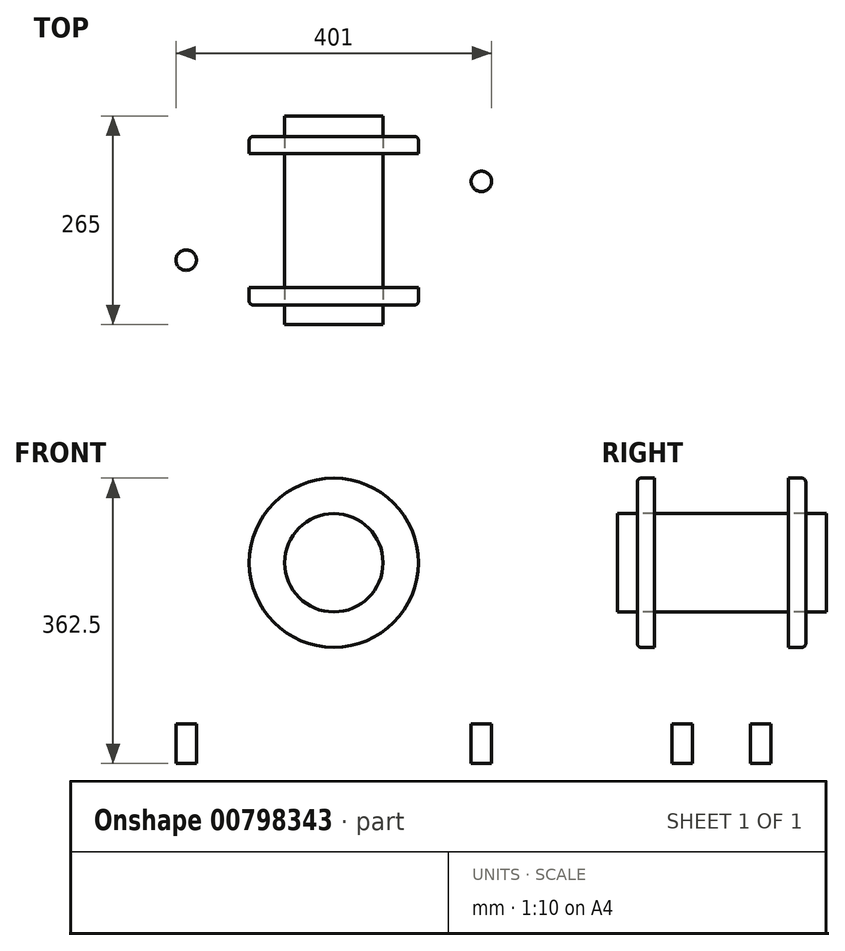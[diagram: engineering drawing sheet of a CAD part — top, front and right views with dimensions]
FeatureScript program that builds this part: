
annotation { "Feature Type Name" : "Feature", "Feature Type Description" : "" }
export const myFeature = defineFeature(function(context is Context, id is Id, definition is map)
    precondition{}
    {
        {
            var Q0;
            Q0=qCreatedBy(makeId("Front.planeOp"),FACE);
            var sketch = newSketch(context, id + "F0", { "sketchPlane" : qUnion([Q0])});
            skCircle(sketch, "E0", {"center": v(0, 0) * mm, "radius": 55 * mm});
            skLineSegment(sketch, "E1.bottom", {"start": v(0, 0) * mm, "end": v(-145, 0) * mm});
            skLineSegment(sketch, "E1.top", {"start": v(0, -255) * mm, "end": v(-225, -255) * mm});
            skLineSegment(sketch, "E1.left", {"start": v(0, 0) * mm, "end": v(0, -255) * mm});
            skLineSegment(sketch, "E1.right", {"start": v(-225, -205) * mm, "end": v(-225, -255) * mm});
            skLineSegment(sketch, "E2.bottom", {"start": v(0, 0) * mm, "end": v(145, 0) * mm});
            skLineSegment(sketch, "E2.top", {"start": v(0, -255) * mm, "end": v(225, -255) * mm});
            skLineSegment(sketch, "E2.right", {"start": v(225, -205) * mm, "end": v(225, -255) * mm});
            skCircle(sketch, "E3", {"center": v(0, 0) * mm, "radius": 90 * mm});
            skLineSegment(sketch, "E4", {"start": v(-145, 0) * mm, "end": v(-145, -205) * mm});
            skLineSegment(sketch, "E5", {"start": v(-145, -205) * mm, "end": v(-225, -205) * mm});
            skLineSegment(sketch, "E6", {"start": v(145, 0) * mm, "end": v(145, -205) * mm});
            skLineSegment(sketch, "E7", {"start": v(145, -205) * mm, "end": v(225, -205) * mm});
            skArc(sketch, "E8", {"start": v(145, 0) * mm, "mid": v(0, 125) * mm, "end": v(-145, 0) * mm});
            skSolve(sketch);
        }
        {
            var Q0;
            {var subQ1=sQuery(id+"F0.wireOp",EDGE,"E2.top");Q0=makeQuery(id+"F0.imprint","IMPRINT",FACE,{"disambiguationData":[TD([[makeQuery(id+"F0.imprint","IMPRINT",EDGE,{"derivedFrom":subQ1}),1.0]])]});}
            var Q1;
            {var subQ0=sQuery(id+"F0.wireOp",EDGE,"E8");Q1=makeQuery(id+"F0.imprint","IMPRINT",FACE,{"disambiguationData":[TD([[makeQuery(id+"F0.imprint","IMPRINT",EDGE,{"derivedFrom":subQ0}),1.0]])]});}
            var Q2;
            {var subQ0=sQuery(id+"F0.wireOp",EDGE,"E1.bottom");var subQ1=sQuery(id+"F0.wireOp",EDGE,"E0");var subQ2=makeQuery(id+"F0.imprint","INTERSECT",VERTEX,{"derivedFrom":[subQ1,subQ0]});Q2=makeQuery(id+"F0.imprint","IMPRINT",FACE,{"disambiguationData":[TD([[makeQuery(id+"F0.imprint","IMPRINT",EDGE,{"disambiguationData":[TD([[subQ2,1.0]])],"derivedFrom":subQ1}),-1.0]])]});}
            var Q3;
            {var subQ1=sQuery(id+"F0.wireOp",EDGE,"E1.top");Q3=makeQuery(id+"F0.imprint","IMPRINT",FACE,{"disambiguationData":[TD([[makeQuery(id+"F0.imprint","IMPRINT",EDGE,{"derivedFrom":subQ1}),-1.0]])]});}
            var Q4;
            {var subQ0=sQuery(id+"F0.wireOp",EDGE,"E1.bottom");var subQ1=sQuery(id+"F0.wireOp",EDGE,"E0");var subQ2=makeQuery(id+"F0.imprint","INTERSECT",VERTEX,{"derivedFrom":[subQ1,subQ0]});Q4=makeQuery(id+"F0.imprint","IMPRINT",FACE,{"disambiguationData":[TD([[makeQuery(id+"F0.imprint","IMPRINT",EDGE,{"disambiguationData":[TD([[subQ2,-1.0]])],"derivedFrom":subQ1}),-1.0]])]});}
            var Q5;
            {var subQ0=sQuery(id+"F0.wireOp",EDGE,"E2.bottom");var subQ1=sQuery(id+"F0.wireOp",EDGE,"E0");var subQ2=makeQuery(id+"F0.imprint","INTERSECT",VERTEX,{"derivedFrom":[subQ1,subQ0]});Q5=makeQuery(id+"F0.imprint","IMPRINT",FACE,{"disambiguationData":[TD([[makeQuery(id+"F0.imprint","IMPRINT",EDGE,{"disambiguationData":[TD([[subQ2,1.0]])],"derivedFrom":subQ1}),-1.0]])]});}
            var Q6;
            {var subQ0=sQuery(id+"F0.wireOp",EDGE,"E2.bottom");var subQ1=sQuery(id+"F0.wireOp",EDGE,"E0");var subQ2=makeQuery(id+"F0.imprint","INTERSECT",VERTEX,{"derivedFrom":[subQ1,subQ0]});Q6=makeQuery(id+"F0.imprint","IMPRINT",FACE,{"disambiguationData":[TD([[makeQuery(id+"F0.imprint","IMPRINT",EDGE,{"disambiguationData":[TD([[subQ2,1.0]])],"derivedFrom":subQ1}),1.0]])]});}
            var Q7;
            {var subQ0=sQuery(id+"F0.wireOp",EDGE,"E1.bottom");var subQ1=sQuery(id+"F0.wireOp",EDGE,"E0");var subQ2=makeQuery(id+"F0.imprint","INTERSECT",VERTEX,{"derivedFrom":[subQ1,subQ0]});Q7=makeQuery(id+"F0.imprint","IMPRINT",FACE,{"disambiguationData":[TD([[makeQuery(id+"F0.imprint","IMPRINT",EDGE,{"disambiguationData":[TD([[subQ2,-1.0]])],"derivedFrom":subQ1}),1.0]])]});}
            var Q8;
            {var subQ0=sQuery(id+"F0.wireOp",EDGE,"E1.bottom");var subQ1=sQuery(id+"F0.wireOp",EDGE,"E0");var subQ2=makeQuery(id+"F0.imprint","INTERSECT",VERTEX,{"derivedFrom":[subQ1,subQ0]});Q8=makeQuery(id+"F0.imprint","IMPRINT",FACE,{"disambiguationData":[TD([[makeQuery(id+"F0.imprint","IMPRINT",EDGE,{"disambiguationData":[TD([[subQ2,1.0]])],"derivedFrom":subQ1}),1.0]])]});}
            extrude(context, id + "F1", {"entities" : qUnion([Q0, Q1, Q2, Q3, Q4, Q5, Q6, Q7, Q8]), "depth" : 170 * mm, "offsetDistance" : 25 * mm});
        }
        {
            var Q0;
            Q0=makeQuery(id+"F1.opExtrude","CAP_FACE",FACE,{"disambiguationData":[OSD([sQuery(id+"F0.wireOp",EDGE,"E1.top"),sQuery(id+"F0.wireOp",EDGE,"E1.right"),sQuery(id+"F0.wireOp",EDGE,"E2.top"),sQuery(id+"F0.wireOp",EDGE,"E2.right"),sQuery(id+"F0.wireOp",EDGE,"E4"),sQuery(id+"F0.wireOp",EDGE,"E5"),sQuery(id+"F0.wireOp",EDGE,"E6"),sQuery(id+"F0.wireOp",EDGE,"E7"),sQuery(id+"F0.wireOp",EDGE,"E8")])],"isStart":true});
            var sketch = newSketch(context, id + "F2", { "sketchPlane" : qUnion([Q0])});
            skCircle(sketch, "E9", {"center": v(0, 0) * mm, "radius": 107.5 * mm});
            skSolve(sketch);
        }
        {
            var Q0;
            Q0=makeQuery(id+"F2.imprint","IMPRINT",FACE,{"disambiguationData":[TD([[makeQuery(id+"F2.imprint","IMPRINT",EDGE,{"derivedFrom":sQuery(id+"F2.wireOp",EDGE,"E9")}),1.0]])]});
            var Q1;
            Q1=sQuery(id+"F2.wireOp",EDGE,"E9");
            extrude(context, id + "F3", {"entities" : qUnion([Q0]), "surfaceEntities" : qUnion([Q1]), "depth" : 22 * mm, "offsetDistance" : 25 * mm});
        }
        {
            var Q0;
            Q0=makeQuery(id+"F1.opExtrude","CAP_FACE",FACE,{"disambiguationData":[OSD([sQuery(id+"F0.wireOp",EDGE,"E1.top"),sQuery(id+"F0.wireOp",EDGE,"E1.right"),sQuery(id+"F0.wireOp",EDGE,"E2.top"),sQuery(id+"F0.wireOp",EDGE,"E2.right"),sQuery(id+"F0.wireOp",EDGE,"E4"),sQuery(id+"F0.wireOp",EDGE,"E5"),sQuery(id+"F0.wireOp",EDGE,"E6"),sQuery(id+"F0.wireOp",EDGE,"E7"),sQuery(id+"F0.wireOp",EDGE,"E8")])],"isStart":false});
            var sketch = newSketch(context, id + "F4", { "sketchPlane" : qUnion([Q0])});
            skCircle(sketch, "E10", {"center": v(0, 0) * mm, "radius": 107.5 * mm});
            skSolve(sketch);
        }
        {
            var Q0;
            Q0=makeQuery(id+"F4.imprint","IMPRINT",FACE,{"disambiguationData":[TD([[makeQuery(id+"F4.imprint","IMPRINT",EDGE,{"derivedFrom":sQuery(id+"F4.wireOp",EDGE,"E10")}),1.0]])]});
            extrude(context, id + "F5", {"entities" : qUnion([Q0]), "operationType" : NewBodyOperationType.ADD, "depth" : 22 * mm, "offsetDistance" : 25 * mm});
        }
        {
            var Q0;
            Q0=makeQuery(id+"F1.opExtrude","SWEPT_FACE",FACE,{"disambiguationData":[OSD([sQuery(id+"F0.wireOp",EDGE,"E1.top"),sQuery(id+"F0.wireOp",EDGE,"E2.top")])]});
            var sketch = newSketch(context, id + "F6", { "sketchPlane" : qUnion([Q0])});
            skLineSegment(sketch, "E11", {"start": v(-225, 85) * mm, "end": v(225, 85) * mm, "construction": true});
            skCircle(sketch, "E12", {"center": v(-187.5, 35) * mm, "radius": 13 * mm});
            skLineSegment(sketch, "E13", {"start": v(0, 0) * mm, "end": v(0, 170) * mm, "construction": true});
            skCircle(sketch, "E14.MirrorC", {"center": v(187.5, 35) * mm, "radius": 13 * mm});
            skLineSegment(sketch, "E15.MirrorCS", {"start": v(225, 85) * mm, "end": v(-225, 85) * mm, "construction": true});
            skCircle(sketch, "E16.MirrorC", {"center": v(-187.5, 135) * mm, "radius": 13 * mm});
            skCircle(sketch, "E17.MirrorC", {"center": v(187.5, 135) * mm, "radius": 13 * mm});
            skSolve(sketch);
        }
        {
            var Q0;
            Q0=makeQuery(id+"F6.imprint","IMPRINT",FACE,{"disambiguationData":[TD([[makeQuery(id+"F6.imprint","IMPRINT",EDGE,{"derivedFrom":sQuery(id+"F6.wireOp",EDGE,"E16.MirrorC")}),-1.0]])]});
            var Q1;
            Q1=makeQuery(id+"F6.imprint","IMPRINT",FACE,{"disambiguationData":[TD([[makeQuery(id+"F6.imprint","IMPRINT",EDGE,{"derivedFrom":sQuery(id+"F6.wireOp",EDGE,"E12")}),1.0]])]});
            var Q2;
            Q2=makeQuery(id+"F6.imprint","IMPRINT",FACE,{"disambiguationData":[TD([[makeQuery(id+"F6.imprint","IMPRINT",EDGE,{"derivedFrom":sQuery(id+"F6.wireOp",EDGE,"E17.MirrorC")}),1.0]])]});
            var Q3;
            Q3=makeQuery(id+"F6.imprint","IMPRINT",FACE,{"disambiguationData":[TD([[makeQuery(id+"F6.imprint","IMPRINT",EDGE,{"derivedFrom":sQuery(id+"F6.wireOp",EDGE,"E14.MirrorC")}),-1.0]])]});
            extrude(context, id + "F7", {"entities" : qUnion([Q0, Q1, Q2, Q3]), "operationType" : NewBodyOperationType.REMOVE, "endBound" : BoundingType.THROUGH_ALL, "oppositeDirection" : true, "depth" : 25 * mm, "offsetDistance" : 25 * mm});
        }
        {
            var Q0;
            Q0=makeQuery(id+"F1.opExtrude","CAP_EDGE",EDGE,{"disambiguationData":[OSD([sQuery(id+"F0.wireOp",EDGE,"E1.right")])],"isStart":true});
            var Q1;
            Q1=makeQuery(id+"F1.opExtrude","CAP_EDGE",EDGE,{"disambiguationData":[OSD([sQuery(id+"F0.wireOp",EDGE,"E1.right")])],"isStart":false});
            var Q2;
            Q2=makeQuery(id+"F1.opExtrude","SWEPT_EDGE",EDGE,{"disambiguationData":[OSD([sQuery(id+"F0.wireOp",EDGE,"E1.right"),sQuery(id+"F0.wireOp",EDGE,"E5")])]});
            var Q3;
            Q3=makeQuery(id+"F1.opExtrude","CAP_EDGE",EDGE,{"disambiguationData":[OSD([sQuery(id+"F0.wireOp",EDGE,"E4")])],"isStart":true});
            var Q4;
            Q4=makeQuery(id+"F1.opExtrude","CAP_EDGE",EDGE,{"disambiguationData":[OSD([sQuery(id+"F0.wireOp",EDGE,"E5")])],"isStart":true});
            var Q5;
            Q5=makeQuery(id+"F1.opExtrude","CAP_EDGE",EDGE,{"disambiguationData":[OSD([sQuery(id+"F0.wireOp",EDGE,"E4")])],"isStart":false});
            var Q6;
            Q6=makeQuery(id+"F1.opExtrude","CAP_EDGE",EDGE,{"disambiguationData":[OSD([sQuery(id+"F0.wireOp",EDGE,"E5")])],"isStart":false});
            var Q7;
            Q7=makeQuery(id+"F1.opExtrude","CAP_EDGE",EDGE,{"disambiguationData":[OSD([sQuery(id+"F0.wireOp",EDGE,"E8")])],"isStart":true});
            var Q8;
            Q8=makeQuery(id+"F1.opExtrude","CAP_EDGE",EDGE,{"disambiguationData":[OSD([sQuery(id+"F0.wireOp",EDGE,"E8")])],"isStart":false});
            var Q9;
            Q9=makeQuery(id+"F1.opExtrude","CAP_EDGE",EDGE,{"disambiguationData":[OSD([sQuery(id+"F0.wireOp",EDGE,"E6")])],"isStart":true});
            var Q10;
            Q10=makeQuery(id+"F1.opExtrude","CAP_EDGE",EDGE,{"disambiguationData":[OSD([sQuery(id+"F0.wireOp",EDGE,"E7")])],"isStart":true});
            var Q11;
            Q11=makeQuery(id+"F1.opExtrude","CAP_EDGE",EDGE,{"disambiguationData":[OSD([sQuery(id+"F0.wireOp",EDGE,"E2.right")])],"isStart":true});
            var Q12;
            Q12=makeQuery(id+"F1.opExtrude","SWEPT_EDGE",EDGE,{"disambiguationData":[OSD([sQuery(id+"F0.wireOp",EDGE,"E2.right"),sQuery(id+"F0.wireOp",EDGE,"E7")])]});
            var Q13;
            Q13=makeQuery(id+"F1.opExtrude","SWEPT_EDGE",EDGE,{"disambiguationData":[OSD([sQuery(id+"F0.wireOp",EDGE,"E6"),sQuery(id+"F0.wireOp",EDGE,"E7")])]});
            var Q14;
            Q14=makeQuery(id+"F1.opExtrude","CAP_EDGE",EDGE,{"disambiguationData":[OSD([sQuery(id+"F0.wireOp",EDGE,"E6")])],"isStart":false});
            var Q15;
            Q15=makeQuery(id+"F1.opExtrude","CAP_EDGE",EDGE,{"disambiguationData":[OSD([sQuery(id+"F0.wireOp",EDGE,"E7")])],"isStart":false});
            var Q16;
            Q16=makeQuery(id+"F1.opExtrude","CAP_EDGE",EDGE,{"disambiguationData":[OSD([sQuery(id+"F0.wireOp",EDGE,"E2.right")])],"isStart":false});
            var Q17;
            Q17=makeQuery(id+"F1.opExtrude","SWEPT_EDGE",EDGE,{"disambiguationData":[OSD([sQuery(id+"F0.wireOp",EDGE,"E4"),sQuery(id+"F0.wireOp",EDGE,"E5")])]});
            var Q18;
            Q18=makeQuery(id+"F3.opExtrude","CAP_EDGE",EDGE,{"disambiguationData":[OSD([sQuery(id+"F2.wireOp",EDGE,"E9")])],"isStart":false});
            var Q19;
            Q19=makeQuery(id+"F5.opExtrude","CAP_EDGE",EDGE,{"disambiguationData":[OSD([sQuery(id+"F4.wireOp",EDGE,"E10")])],"isStart":false});
            fillet(context, id + "F8", {"entities" : qUnion([Q0, Q1, Q2, Q3, Q4, Q5, Q6, Q7, Q8, Q9, Q10, Q11, Q12, Q13, Q14, Q15, Q16, Q17, Q18, Q19]), "radius" : 5 * mm, "tangentPropagation" : true, "allowEdgeOverflow" : false});
        }
        {
            var Q0;
            Q0=makeQuery(id+"F5.opExtrude","CAP_FACE",FACE,{"disambiguationData":[OSD([sQuery(id+"F4.wireOp",EDGE,"E10")])],"isStart":false});
            var sketch = newSketch(context, id + "F9", { "sketchPlane" : qUnion([Q0])});
            skCircle(sketch, "E18", {"center": v(0, 0) * mm, "radius": 62.5 * mm});
            skSolve(sketch);
        }
        {
            var Q0;
            Q0=makeQuery(id+"F9.imprint","IMPRINT",FACE,{"disambiguationData":[TD([[makeQuery(id+"F9.imprint","IMPRINT",EDGE,{"derivedFrom":sQuery(id+"F9.wireOp",EDGE,"E18")}),1.0]])]});
            extrude(context, id + "F10", {"entities" : qUnion([Q0]), "oppositeDirection" : true, "depth" : 240 * mm, "offsetDistance" : 25 * mm, "hasSecondDirection" : true, "secondDirectionOppositeDirection" : false, "secondDirectionDepth" : 25 * mm});
        }
    });
